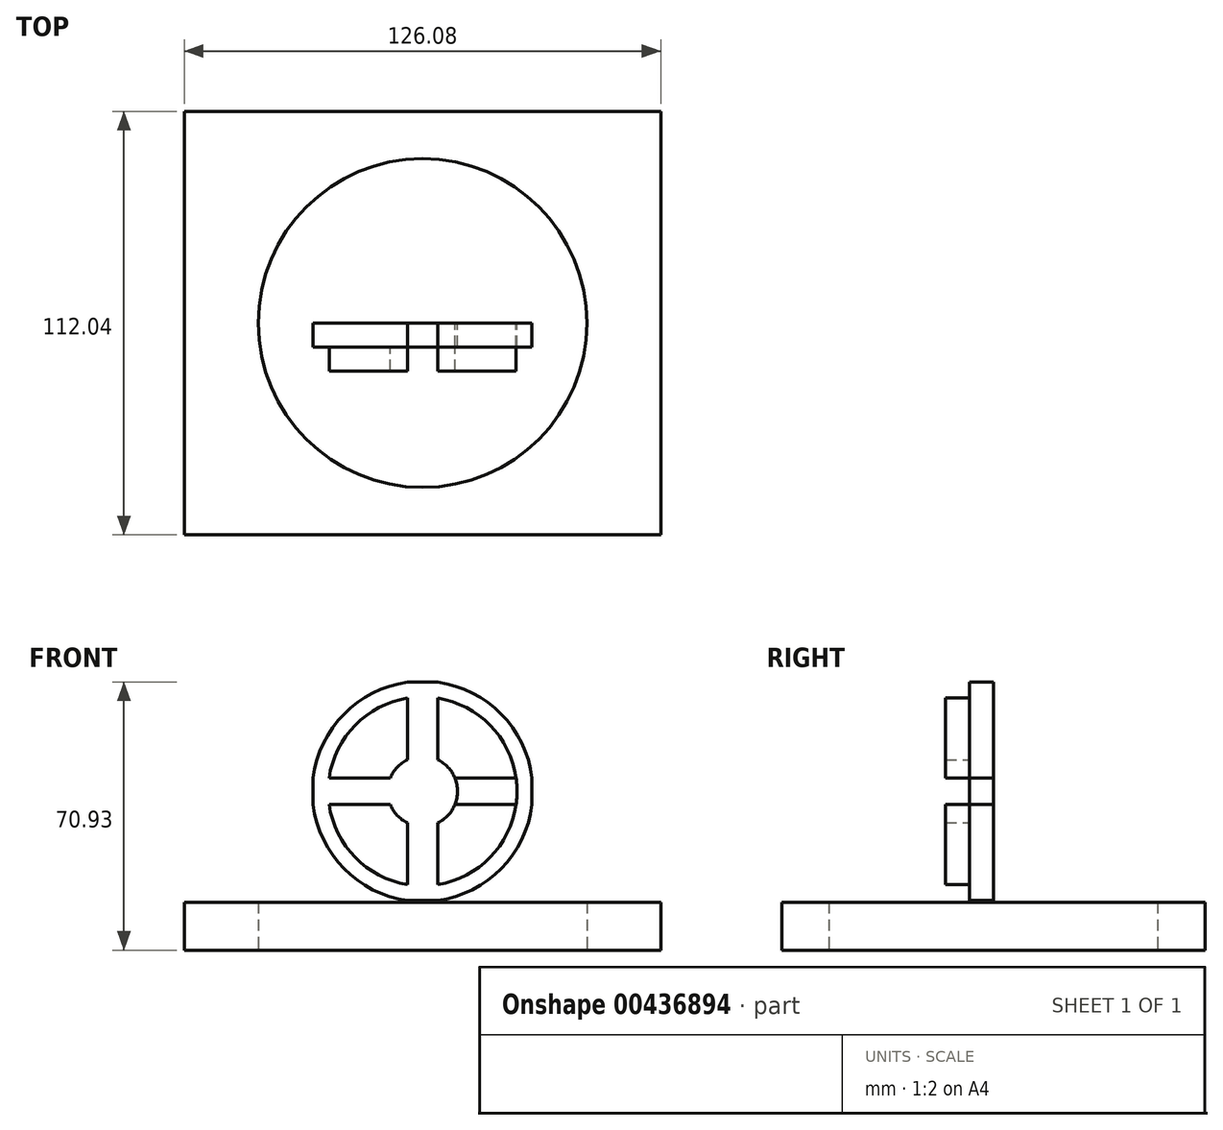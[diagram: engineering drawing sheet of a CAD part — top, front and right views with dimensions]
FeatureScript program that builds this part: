
annotation { "Feature Type Name" : "Feature", "Feature Type Description" : "" }
export const myFeature = defineFeature(function(context is Context, id is Id, definition is map)
    precondition{}
    {
        {
            var Q0;
            Q0=qCreatedBy(makeId("Top.planeOp"),FACE);
            var sketch = newSketch(context, id + "F0", { "sketchPlane" : qUnion([Q0])});
            skLineSegment(sketch, "E0.bottom", {"start": v(-63.04, 56.02) * mm, "end": v(63.04, 56.02) * mm});
            skLineSegment(sketch, "E0.top", {"start": v(-63.04, -56.02) * mm, "end": v(63.04, -56.02) * mm});
            skLineSegment(sketch, "E0.left", {"start": v(-63.04, 56.02) * mm, "end": v(-63.04, -56.02) * mm});
            skLineSegment(sketch, "E0.right", {"start": v(63.04, 56.02) * mm, "end": v(63.04, -56.02) * mm});
            skPoint(sketch, "E0.middle", {"position": v(0, 0) * mm});
            skCircle(sketch, "E1", {"center": v(0, 0) * mm, "radius": 43.49 * mm});
            skSolve(sketch);
        }
        {
            var Q0;
            Q0=makeQuery(id+"F0.imprint","IMPRINT",FACE,{"disambiguationData":[TD([[makeQuery(id+"F0.imprint","IMPRINT",EDGE,{"derivedFrom":sQuery(id+"F0.wireOp",EDGE,"E1")}),1.0]])]});
            var Q1;
            Q1=makeQuery(id+"F0.imprint","IMPRINT",FACE,{"disambiguationData":[TD([[makeQuery(id+"F0.imprint","IMPRINT",EDGE,{"derivedFrom":sQuery(id+"F0.wireOp",EDGE,"E0.bottom")}),-1.0]])]});
            extrude(context, id + "F1", {"entities" : qUnion([Q0, Q1]), "depth" : 12.7 * mm});
        }
        {
            var Q0;
            Q0=qCreatedBy(makeId("Front.planeOp"),FACE);
            var sketch = newSketch(context, id + "F2", { "sketchPlane" : qUnion([Q0])});
            skCircle(sketch, "E2", {"center": v(0, 42.03) * mm, "radius": 29.18 * mm});
            skLineSegment(sketch, "E3.bottom", {"start": v(-4, 70.93) * mm, "end": v(4, 70.93) * mm});
            skLineSegment(sketch, "E3.top", {"start": v(-4, 13.13) * mm, "end": v(4, 13.13) * mm});
            skLineSegment(sketch, "E3.left", {"start": v(-4, 70.93) * mm, "end": v(-4, 13.13) * mm});
            skLineSegment(sketch, "E3.right", {"start": v(4, 70.93) * mm, "end": v(4, 13.13) * mm});
            skLineSegment(sketch, "E4.bottom", {"start": v(-28.96, 38.5) * mm, "end": v(28.96, 38.5) * mm});
            skLineSegment(sketch, "E4.top", {"start": v(-28.96, 45.56) * mm, "end": v(28.96, 45.56) * mm});
            skLineSegment(sketch, "E4.left", {"start": v(-28.96, 38.5) * mm, "end": v(-28.96, 45.56) * mm});
            skLineSegment(sketch, "E4.right", {"start": v(28.96, 38.5) * mm, "end": v(28.96, 45.56) * mm});
            skCircle(sketch, "E5", {"center": v(0, 42.03) * mm, "radius": 24.99 * mm});
            skCircle(sketch, "E6", {"center": v(0, 42.03) * mm, "radius": 9.26 * mm});
            skSolve(sketch);
        }
        {
            var Q0;
            {var subQ0=sQuery(id+"F2.wireOp",EDGE,"E3.left");var subQ5=sQuery(id+"F2.wireOp",EDGE,"E5");var subQ6=makeQuery(id+"F2.imprint","INTERSECT",VERTEX,{"disambiguationData":[OD(0.0)],"derivedFrom":[subQ0,subQ5]});Q0=makeQuery(id+"F2.imprint","IMPRINT",FACE,{"disambiguationData":[TD([[makeQuery(id+"F2.imprint","IMPRINT",EDGE,{"disambiguationData":[TD([[subQ6,-1.0]])],"derivedFrom":subQ5}),-1.0]])]});}
            var Q1;
            {var subQ0=sQuery(id+"F2.wireOp",EDGE,"E3.left");var subQ5=sQuery(id+"F2.wireOp",EDGE,"E5");var subQ7=makeQuery(id+"F2.imprint","INTERSECT",VERTEX,{"disambiguationData":[OD(1.0)],"derivedFrom":[subQ0,subQ5]});Q1=makeQuery(id+"F2.imprint","IMPRINT",FACE,{"disambiguationData":[TD([[makeQuery(id+"F2.imprint","IMPRINT",EDGE,{"disambiguationData":[TD([[subQ7,1.0]])],"derivedFrom":subQ5}),-1.0]])]});}
            var Q2;
            {var subQ0=sQuery(id+"F2.wireOp",EDGE,"E4.left");Q2=makeQuery(id+"F2.imprint","IMPRINT",FACE,{"disambiguationData":[TD([[makeQuery(id+"F2.imprint","IMPRINT",EDGE,{"derivedFrom":subQ0}),-1.0]])]});}
            var Q3;
            {var subQ0=sQuery(id+"F2.wireOp",EDGE,"E3.top");Q3=makeQuery(id+"F2.imprint","IMPRINT",FACE,{"disambiguationData":[TD([[makeQuery(id+"F2.imprint","IMPRINT",EDGE,{"derivedFrom":subQ0}),1.0]])]});}
            var Q4;
            {var subQ0=sQuery(id+"F2.wireOp",EDGE,"E3.right");var subQ5=sQuery(id+"F2.wireOp",EDGE,"E5");var subQ6=makeQuery(id+"F2.imprint","INTERSECT",VERTEX,{"disambiguationData":[OD(1.0)],"derivedFrom":[subQ0,subQ5]});Q4=makeQuery(id+"F2.imprint","IMPRINT",FACE,{"disambiguationData":[TD([[makeQuery(id+"F2.imprint","IMPRINT",EDGE,{"disambiguationData":[TD([[subQ6,-1.0]])],"derivedFrom":subQ5}),-1.0]])]});}
            var Q5;
            {var subQ0=sQuery(id+"F2.wireOp",EDGE,"E3.right");var subQ5=sQuery(id+"F2.wireOp",EDGE,"E5");var subQ6=makeQuery(id+"F2.imprint","INTERSECT",VERTEX,{"disambiguationData":[OD(0.0)],"derivedFrom":[subQ0,subQ5]});Q5=makeQuery(id+"F2.imprint","IMPRINT",FACE,{"disambiguationData":[TD([[makeQuery(id+"F2.imprint","IMPRINT",EDGE,{"disambiguationData":[TD([[subQ6,1.0]])],"derivedFrom":subQ5}),-1.0]])]});}
            var Q6;
            {var subQ0=sQuery(id+"F2.wireOp",EDGE,"E3.bottom");Q6=makeQuery(id+"F2.imprint","IMPRINT",FACE,{"disambiguationData":[TD([[makeQuery(id+"F2.imprint","IMPRINT",EDGE,{"derivedFrom":subQ0}),-1.0]])]});}
            var Q7;
            {var subQ0=sQuery(id+"F2.wireOp",EDGE,"E4.right");Q7=makeQuery(id+"F2.imprint","IMPRINT",FACE,{"disambiguationData":[TD([[makeQuery(id+"F2.imprint","IMPRINT",EDGE,{"derivedFrom":subQ0}),1.0]])]});}
            var Q8;
            {var subQ0=sQuery(id+"F2.wireOp",EDGE,"E5");var subQ1=sQuery(id+"F2.wireOp",EDGE,"E3.left");var subQ2=makeQuery(id+"F2.imprint","INTERSECT",VERTEX,{"disambiguationData":[OD(0.0)],"derivedFrom":[subQ1,subQ0]});Q8=makeQuery(id+"F2.imprint","IMPRINT",FACE,{"disambiguationData":[TD([[makeQuery(id+"F2.imprint","IMPRINT",EDGE,{"disambiguationData":[TD([[subQ2,-1.0]])],"derivedFrom":subQ1}),1.0]])]});}
            var Q9;
            {var subQ0=sQuery(id+"F2.wireOp",EDGE,"E6");var subQ1=sQuery(id+"F2.wireOp",EDGE,"E3.left");var subQ2=makeQuery(id+"F2.imprint","INTERSECT",VERTEX,{"disambiguationData":[OD(0.0)],"derivedFrom":[subQ1,subQ0]});Q9=makeQuery(id+"F2.imprint","IMPRINT",FACE,{"disambiguationData":[TD([[makeQuery(id+"F2.imprint","IMPRINT",EDGE,{"disambiguationData":[TD([[subQ2,-1.0]])],"derivedFrom":subQ1}),1.0]])]});}
            var Q10;
            {var subQ0=sQuery(id+"F2.wireOp",EDGE,"E4.top");var subQ1=sQuery(id+"F2.wireOp",EDGE,"E3.left");var subQ2=makeQuery(id+"F2.imprint","INTERSECT",VERTEX,{"derivedFrom":[subQ1,subQ0]});Q10=makeQuery(id+"F2.imprint","IMPRINT",FACE,{"disambiguationData":[TD([[makeQuery(id+"F2.imprint","IMPRINT",EDGE,{"disambiguationData":[TD([[subQ2,-1.0]])],"derivedFrom":subQ1}),1.0]])]});}
            var Q11;
            {var subQ0=sQuery(id+"F2.wireOp",EDGE,"E4.bottom");var subQ1=sQuery(id+"F2.wireOp",EDGE,"E3.left");var subQ2=makeQuery(id+"F2.imprint","INTERSECT",VERTEX,{"derivedFrom":[subQ1,subQ0]});Q11=makeQuery(id+"F2.imprint","IMPRINT",FACE,{"disambiguationData":[TD([[makeQuery(id+"F2.imprint","IMPRINT",EDGE,{"disambiguationData":[TD([[subQ2,-1.0]])],"derivedFrom":subQ1}),1.0]])]});}
            var Q12;
            {var subQ0=sQuery(id+"F2.wireOp",EDGE,"E4.top");var subQ1=sQuery(id+"F2.wireOp",EDGE,"E3.right");var subQ2=makeQuery(id+"F2.imprint","INTERSECT",VERTEX,{"derivedFrom":[subQ1,subQ0]});Q12=makeQuery(id+"F2.imprint","IMPRINT",FACE,{"disambiguationData":[TD([[makeQuery(id+"F2.imprint","IMPRINT",EDGE,{"disambiguationData":[TD([[subQ2,-1.0]])],"derivedFrom":subQ1}),1.0]])]});}
            var Q13;
            {var subQ0=sQuery(id+"F2.wireOp",EDGE,"E6");var subQ1=sQuery(id+"F2.wireOp",EDGE,"E3.right");var subQ2=makeQuery(id+"F2.imprint","INTERSECT",VERTEX,{"disambiguationData":[OD(0.0)],"derivedFrom":[subQ1,subQ0]});Q13=makeQuery(id+"F2.imprint","IMPRINT",FACE,{"disambiguationData":[TD([[makeQuery(id+"F2.imprint","IMPRINT",EDGE,{"disambiguationData":[TD([[subQ2,-1.0]])],"derivedFrom":subQ1}),1.0]])]});}
            var Q14;
            {var subQ0=sQuery(id+"F2.wireOp",EDGE,"E4.bottom");var subQ1=sQuery(id+"F2.wireOp",EDGE,"E3.right");var subQ2=makeQuery(id+"F2.imprint","INTERSECT",VERTEX,{"derivedFrom":[subQ1,subQ0]});Q14=makeQuery(id+"F2.imprint","IMPRINT",FACE,{"disambiguationData":[TD([[makeQuery(id+"F2.imprint","IMPRINT",EDGE,{"disambiguationData":[TD([[subQ2,-1.0]])],"derivedFrom":subQ1}),1.0]])]});}
            var Q15;
            {var subQ0=sQuery(id+"F2.wireOp",EDGE,"E4.bottom");var subQ1=sQuery(id+"F2.wireOp",EDGE,"E3.left");var subQ2=makeQuery(id+"F2.imprint","INTERSECT",VERTEX,{"derivedFrom":[subQ1,subQ0]});Q15=makeQuery(id+"F2.imprint","IMPRINT",FACE,{"disambiguationData":[TD([[makeQuery(id+"F2.imprint","IMPRINT",EDGE,{"disambiguationData":[TD([[subQ2,-1.0]])],"derivedFrom":subQ1}),-1.0]])]});}
            var Q16;
            {var subQ0=sQuery(id+"F2.wireOp",EDGE,"E4.top");var subQ1=sQuery(id+"F2.wireOp",EDGE,"E3.left");var subQ2=makeQuery(id+"F2.imprint","INTERSECT",VERTEX,{"derivedFrom":[subQ1,subQ0]});Q16=makeQuery(id+"F2.imprint","IMPRINT",FACE,{"disambiguationData":[TD([[makeQuery(id+"F2.imprint","IMPRINT",EDGE,{"disambiguationData":[TD([[subQ2,-1.0]])],"derivedFrom":subQ1}),-1.0]])]});}
            var Q17;
            {var subQ0=sQuery(id+"F2.wireOp",EDGE,"E6");var subQ1=sQuery(id+"F2.wireOp",EDGE,"E3.left");var subQ2=makeQuery(id+"F2.imprint","INTERSECT",VERTEX,{"disambiguationData":[OD(0.0)],"derivedFrom":[subQ1,subQ0]});Q17=makeQuery(id+"F2.imprint","IMPRINT",FACE,{"disambiguationData":[TD([[makeQuery(id+"F2.imprint","IMPRINT",EDGE,{"disambiguationData":[TD([[subQ2,-1.0]])],"derivedFrom":subQ1}),-1.0]])]});}
            var Q18;
            {var subQ0=sQuery(id+"F2.wireOp",EDGE,"E5");var subQ1=sQuery(id+"F2.wireOp",EDGE,"E4.bottom");var subQ2=makeQuery(id+"F2.imprint","INTERSECT",VERTEX,{"disambiguationData":[OD(0.0)],"derivedFrom":[subQ1,subQ0]});Q18=makeQuery(id+"F2.imprint","IMPRINT",FACE,{"disambiguationData":[TD([[makeQuery(id+"F2.imprint","IMPRINT",EDGE,{"disambiguationData":[TD([[subQ2,-1.0]])],"derivedFrom":subQ1}),1.0]])]});}
            var Q19;
            {var subQ0=sQuery(id+"F2.wireOp",EDGE,"E6");var subQ1=sQuery(id+"F2.wireOp",EDGE,"E3.left");var subQ2=makeQuery(id+"F2.imprint","INTERSECT",VERTEX,{"disambiguationData":[OD(1.0)],"derivedFrom":[subQ1,subQ0]});Q19=makeQuery(id+"F2.imprint","IMPRINT",FACE,{"disambiguationData":[TD([[makeQuery(id+"F2.imprint","IMPRINT",EDGE,{"disambiguationData":[TD([[subQ2,-1.0]])],"derivedFrom":subQ1}),1.0]])]});}
            var Q20;
            {var subQ0=sQuery(id+"F2.wireOp",EDGE,"E6");var subQ1=sQuery(id+"F2.wireOp",EDGE,"E4.bottom");var subQ2=makeQuery(id+"F2.imprint","INTERSECT",VERTEX,{"disambiguationData":[OD(1.0)],"derivedFrom":[subQ1,subQ0]});Q20=makeQuery(id+"F2.imprint","IMPRINT",FACE,{"disambiguationData":[TD([[makeQuery(id+"F2.imprint","IMPRINT",EDGE,{"disambiguationData":[TD([[subQ2,-1.0]])],"derivedFrom":subQ1}),1.0]])]});}
            extrude(context, id + "F3", {"entities" : qUnion([Q0, Q1, Q2, Q3, Q4, Q5, Q6, Q7, Q8, Q9, Q10, Q11, Q12, Q13, Q14, Q15, Q16, Q17, Q18, Q19, Q20]), "depth" : 6.35 * mm});
        }
        {
            var Q0;
            Q0=makeQuery(id+"F3.opExtrude","CAP_FACE",FACE,{"disambiguationData":[OSD([sQuery(id+"F2.wireOp",EDGE,"E2"),sQuery(id+"F2.wireOp",EDGE,"E3.bottom"),sQuery(id+"F2.wireOp",EDGE,"E3.top"),sQuery(id+"F2.wireOp",EDGE,"E3.left"),sQuery(id+"F2.wireOp",EDGE,"E3.right"),sQuery(id+"F2.wireOp",EDGE,"E4.bottom"),sQuery(id+"F2.wireOp",EDGE,"E4.top"),sQuery(id+"F2.wireOp",EDGE,"E4.left"),sQuery(id+"F2.wireOp",EDGE,"E4.right"),sQuery(id+"F2.wireOp",EDGE,"E5"),sQuery(id+"F2.wireOp",EDGE,"E6")])],"isStart":false});
            extrude(context, id + "F4", {"entities" : qUnion([Q0]), "operationType" : NewBodyOperationType.ADD, "depth" : -6.35 * mm});
        }
        {
            var Q0;
            {var subQ0=sQuery(id+"F2.wireOp",EDGE,"E5");var subQ1=sQuery(id+"F2.wireOp",EDGE,"E3.left");var subQ2=makeQuery(id+"F2.imprint","INTERSECT",VERTEX,{"disambiguationData":[OD(0.0)],"derivedFrom":[subQ1,subQ0]});Q0=makeQuery(id+"F2.imprint","IMPRINT",FACE,{"disambiguationData":[TD([[makeQuery(id+"F2.imprint","IMPRINT",EDGE,{"disambiguationData":[TD([[subQ2,-1.0]])],"derivedFrom":subQ1}),-1.0]])]});}
            var Q1;
            {var subQ0=sQuery(id+"F2.wireOp",EDGE,"E5");var subQ1=sQuery(id+"F2.wireOp",EDGE,"E3.right");var subQ2=makeQuery(id+"F2.imprint","INTERSECT",VERTEX,{"disambiguationData":[OD(0.0)],"derivedFrom":[subQ1,subQ0]});Q1=makeQuery(id+"F2.imprint","IMPRINT",FACE,{"disambiguationData":[TD([[makeQuery(id+"F2.imprint","IMPRINT",EDGE,{"disambiguationData":[TD([[subQ2,-1.0]])],"derivedFrom":subQ1}),1.0]])]});}
            var Q2;
            {var subQ0=sQuery(id+"F2.wireOp",EDGE,"E6");var subQ1=sQuery(id+"F2.wireOp",EDGE,"E3.right");var subQ2=makeQuery(id+"F2.imprint","INTERSECT",VERTEX,{"disambiguationData":[OD(1.0)],"derivedFrom":[subQ1,subQ0]});Q2=makeQuery(id+"F2.imprint","IMPRINT",FACE,{"disambiguationData":[TD([[makeQuery(id+"F2.imprint","IMPRINT",EDGE,{"disambiguationData":[TD([[subQ2,-1.0]])],"derivedFrom":subQ1}),1.0]])]});}
            var Q3;
            {var subQ0=sQuery(id+"F2.wireOp",EDGE,"E6");var subQ1=sQuery(id+"F2.wireOp",EDGE,"E3.left");var subQ2=makeQuery(id+"F2.imprint","INTERSECT",VERTEX,{"disambiguationData":[OD(1.0)],"derivedFrom":[subQ1,subQ0]});Q3=makeQuery(id+"F2.imprint","IMPRINT",FACE,{"disambiguationData":[TD([[makeQuery(id+"F2.imprint","IMPRINT",EDGE,{"disambiguationData":[TD([[subQ2,-1.0]])],"derivedFrom":subQ1}),-1.0]])]});}
            extrude(context, id + "F5", {"entities" : qUnion([Q0, Q1, Q2, Q3]), "operationType" : NewBodyOperationType.ADD, "depth" : 12.7 * mm});
        }
        {
            var Q0;
            {var subQ0=sQuery(id+"F2.wireOp",EDGE,"E5");var subQ1=sQuery(id+"F2.wireOp",EDGE,"E3.right");var subQ2=makeQuery(id+"F2.imprint","INTERSECT",VERTEX,{"disambiguationData":[OD(0.0)],"derivedFrom":[subQ1,subQ0]});Q0=makeQuery(id+"F2.imprint","IMPRINT",FACE,{"disambiguationData":[TD([[makeQuery(id+"F2.imprint","IMPRINT",EDGE,{"disambiguationData":[TD([[subQ2,-1.0]])],"derivedFrom":subQ1}),1.0]])]});}
            var Q1;
            {var subQ0=sQuery(id+"F2.wireOp",EDGE,"E5");var subQ1=sQuery(id+"F2.wireOp",EDGE,"E3.left");var subQ2=makeQuery(id+"F2.imprint","INTERSECT",VERTEX,{"disambiguationData":[OD(0.0)],"derivedFrom":[subQ1,subQ0]});Q1=makeQuery(id+"F2.imprint","IMPRINT",FACE,{"disambiguationData":[TD([[makeQuery(id+"F2.imprint","IMPRINT",EDGE,{"disambiguationData":[TD([[subQ2,-1.0]])],"derivedFrom":subQ1}),-1.0]])]});}
            var Q2;
            {var subQ0=sQuery(id+"F2.wireOp",EDGE,"E6");var subQ1=sQuery(id+"F2.wireOp",EDGE,"E3.left");var subQ2=makeQuery(id+"F2.imprint","INTERSECT",VERTEX,{"disambiguationData":[OD(1.0)],"derivedFrom":[subQ1,subQ0]});Q2=makeQuery(id+"F2.imprint","IMPRINT",FACE,{"disambiguationData":[TD([[makeQuery(id+"F2.imprint","IMPRINT",EDGE,{"disambiguationData":[TD([[subQ2,-1.0]])],"derivedFrom":subQ1}),-1.0]])]});}
            var Q3;
            {var subQ0=sQuery(id+"F2.wireOp",EDGE,"E6");var subQ1=sQuery(id+"F2.wireOp",EDGE,"E3.right");var subQ2=makeQuery(id+"F2.imprint","INTERSECT",VERTEX,{"disambiguationData":[OD(1.0)],"derivedFrom":[subQ1,subQ0]});Q3=makeQuery(id+"F2.imprint","IMPRINT",FACE,{"disambiguationData":[TD([[makeQuery(id+"F2.imprint","IMPRINT",EDGE,{"disambiguationData":[TD([[subQ2,-1.0]])],"derivedFrom":subQ1}),1.0]])]});}
            extrude(context, id + "F6", {"entities" : qUnion([Q0, Q1, Q2, Q3]), "operationType" : NewBodyOperationType.ADD, "depth" : 6.35 * mm});
        }
        {
            var Q0;
            Q0=makeQuery(id+"F0.imprint","IMPRINT",FACE,{"disambiguationData":[TD([[makeQuery(id+"F0.imprint","IMPRINT",EDGE,{"derivedFrom":sQuery(id+"F0.wireOp",EDGE,"E1")}),1.0]])]});
            extrude(context, id + "F7", {"entities" : qUnion([Q0]), "depth" : 12.7 * mm});
        }
    });
